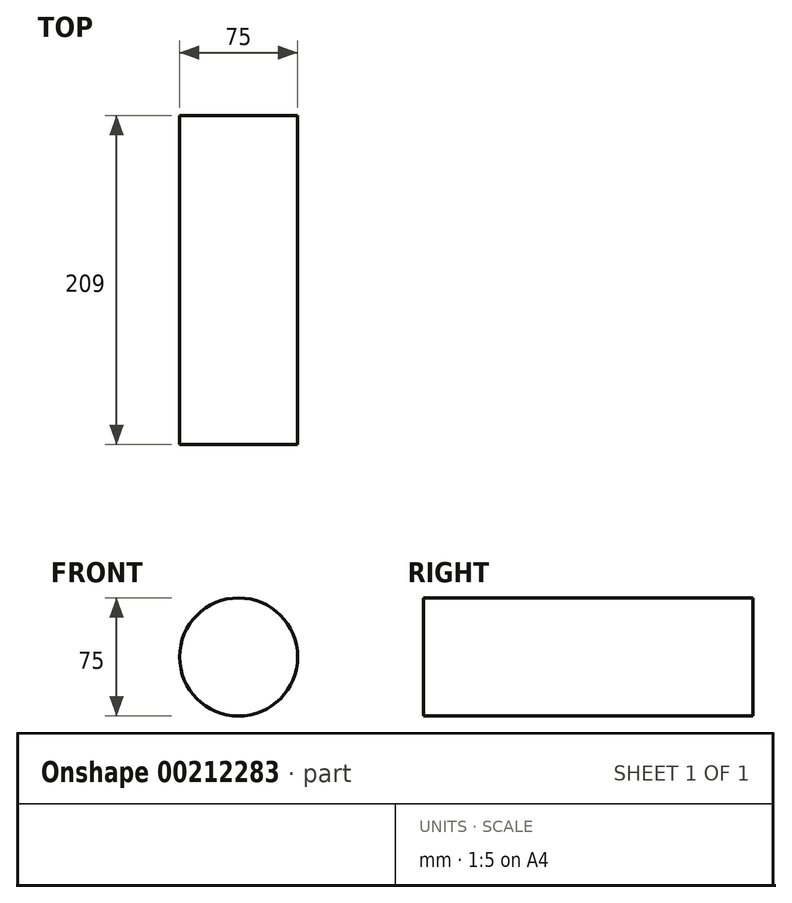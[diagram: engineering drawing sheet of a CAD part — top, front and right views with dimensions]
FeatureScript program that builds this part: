
annotation { "Feature Type Name" : "Feature", "Feature Type Description" : "" }
export const myFeature = defineFeature(function(context is Context, id is Id, definition is map)
    precondition{}
    {
        {
            var Q0;
            Q0=qCreatedBy(makeId("Front.planeOp"),FACE);
            var sketch = newSketch(context, id + "F0", { "sketchPlane" : qUnion([Q0])});
            skCircle(sketch, "E0", {"center": v(-33.87, 23.83) * mm, "radius": 37.5 * mm});
            skSolve(sketch);
        }
        {
            var Q0;
            Q0=makeQuery(id+"F0.imprint","IMPRINT",FACE,{"disambiguationData":[TD([[makeQuery(id+"F0.imprint","IMPRINT",EDGE,{"derivedFrom":sQuery(id+"F0.wireOp",EDGE,"E0")}),1.0]])]});
            extrude(context, id + "F1", {"entities" : qUnion([Q0]), "depth" : 209 * mm});
        }
    });
